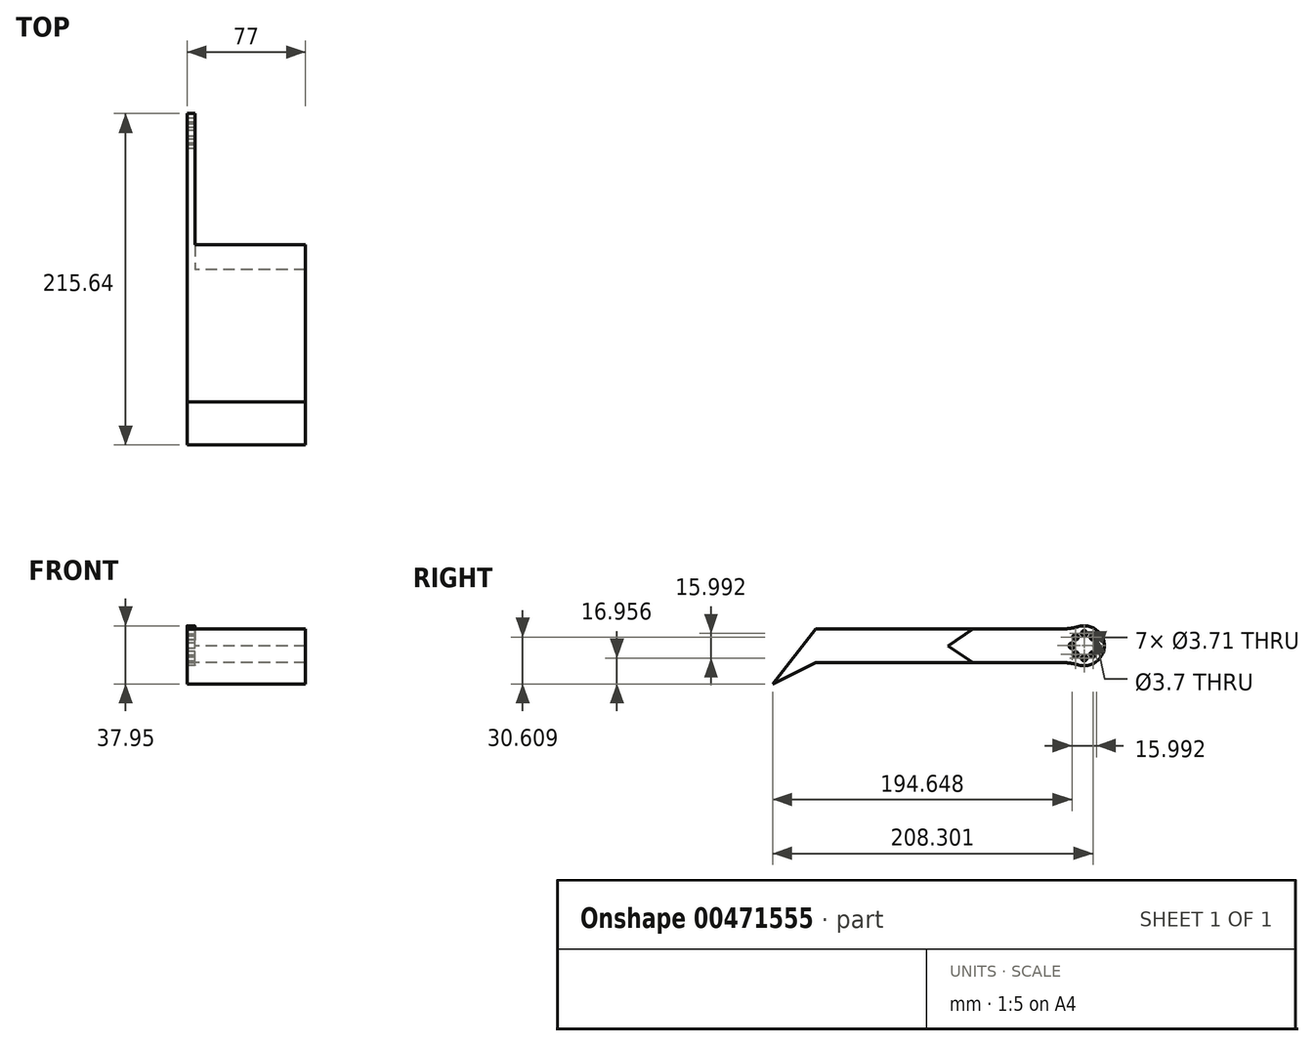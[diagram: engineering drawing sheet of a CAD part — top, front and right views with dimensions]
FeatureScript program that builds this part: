
annotation { "Feature Type Name" : "Feature", "Feature Type Description" : "" }
export const myFeature = defineFeature(function(context is Context, id is Id, definition is map)
    precondition{}
    {
        {
            var Q0;
            Q0=qCreatedBy(makeId("Right.planeOp"),FACE);
            var sketch = newSketch(context, id + "F0", { "sketchPlane" : qUnion([Q0])});
            skLineSegment(sketch, "E0", {"start": v(-42.2, 31.52) * mm, "end": v(60, 31.52) * mm});
            skLineSegment(sketch, "E1", {"start": v(-70.23, -4.43) * mm, "end": v(-42.2, 31.52) * mm});
            skLineSegment(sketch, "E2", {"start": v(-70.23, -4.43) * mm, "end": v(-42.2, 9.51) * mm});
            skLineSegment(sketch, "E3", {"start": v(-42.2, 9.51) * mm, "end": v(60.02, 9.51) * mm});
            skLineSegment(sketch, "E4", {"start": v(60, 31.52) * mm, "end": v(44.03, 20.52) * mm});
            skLineSegment(sketch, "E5", {"start": v(60.02, 9.51) * mm, "end": v(44.03, 20.52) * mm});
            skLineSegment(sketch, "E6", {"start": v(-42.2, 31.52) * mm, "end": v(-42.2, 9.51) * mm, "construction": true});
            skSolve(sketch);
        }
        {
            var Q0;
            Q0=qCreatedBy(makeId("Right.planeOp"),FACE);
            var sketch = newSketch(context, id + "F1", { "sketchPlane" : qUnion([Q0])});
            skLineSegment(sketch, "E7", {"start": v(60, 31.52) * mm, "end": v(125.49, 31.52) * mm});
            skLineSegment(sketch, "E8", {"start": v(125.5, 9.51) * mm, "end": v(60.02, 9.51) * mm});
            skLineSegment(sketch, "E9", {"start": v(60, 31.52) * mm, "end": v(44.03, 20.52) * mm});
            skLineSegment(sketch, "E10", {"start": v(60.02, 9.51) * mm, "end": v(44.03, 20.52) * mm});
            skCircle(sketch, "E11", {"center": v(132.41, 20.52) * mm, "radius": 13 * mm});
            skPoint(sketch, "E11.third.point", {"position": v(145.35, 21.86) * mm});
            skLineSegment(sketch, "E12", {"start": v(132.41, 51.7) * mm, "end": v(132.41, 20.52) * mm, "construction": true});
            skCircle(sketch, "E13", {"center": v(132.41, 28.52) * mm, "radius": 1.85 * mm});
            skPoint(sketch, "E13.first.point", {"position": v(132.41, 30.37) * mm});
            skPoint(sketch, "E13.second.point", {"position": v(132.41, 26.67) * mm});
            skPoint(sketch, "E13.third.point", {"position": v(134.26, 28.4) * mm});
            skLineSegment(sketch, "E14", {"start": v(132.41, 28.52) * mm, "end": v(132.41, 20.52) * mm, "construction": true});
            skLineSegment(sketch, "E15", {"start": v(132.41, 33.52) * mm, "end": v(132.41, 26.67) * mm, "construction": true});
            skLineSegment(sketch, "E16", {"start": v(132.41, 20.52) * mm, "end": v(132.41, 7.52) * mm, "construction": true});
            skCircle(sketch, "E17", {"center": v(132.41, 12.53) * mm, "radius": 1.85 * mm});
            skPoint(sketch, "E17.first.point", {"position": v(132.41, 14.38) * mm});
            skPoint(sketch, "E17.second.point", {"position": v(132.41, 10.67) * mm});
            skPoint(sketch, "E17.third.point", {"position": v(134.26, 12.65) * mm});
            skLineSegment(sketch, "E18", {"start": v(132.41, 14.38) * mm, "end": v(132.41, 12.53) * mm, "construction": true});
            skLineSegment(sketch, "E19", {"start": v(132.41, 14.38) * mm, "end": v(132.41, 7.52) * mm, "construction": true});
            skLineSegment(sketch, "E20", {"start": v(132.41, 20.52) * mm, "end": v(145.41, 20.52) * mm, "construction": true});
            skLineSegment(sketch, "E21", {"start": v(132.41, 20.52) * mm, "end": v(119.41, 20.52) * mm, "construction": true});
            skCircle(sketch, "E22", {"center": v(140.41, 20.52) * mm, "radius": 1.85 * mm});
            skPoint(sketch, "E22.first.point", {"position": v(138.56, 20.52) * mm});
            skPoint(sketch, "E22.second.point", {"position": v(142.26, 20.52) * mm});
            skPoint(sketch, "E22.third.point", {"position": v(140.32, 22.37) * mm});
            skLineSegment(sketch, "E23", {"start": v(140.41, 20.52) * mm, "end": v(132.41, 20.52) * mm, "construction": true});
            skLineSegment(sketch, "E24", {"start": v(138.56, 20.52) * mm, "end": v(145.41, 20.52) * mm, "construction": true});
            skCircle(sketch, "E25", {"center": v(124.42, 20.52) * mm, "radius": 1.85 * mm});
            skPoint(sketch, "E25.first.point", {"position": v(122.56, 20.52) * mm});
            skPoint(sketch, "E25.second.point", {"position": v(126.27, 20.52) * mm});
            skPoint(sketch, "E25.third.point", {"position": v(124.67, 22.36) * mm});
            skLineSegment(sketch, "E26", {"start": v(124.42, 20.52) * mm, "end": v(119.41, 20.52) * mm, "construction": true});
            skLineSegment(sketch, "E27", {"start": v(119.41, 20.52) * mm, "end": v(126.27, 20.52) * mm, "construction": true});
            skPoint(sketch, "E28.1.0", {"position": v(129.34, 25.84) * mm});
            skPoint(sketch, "E28.2.0", {"position": v(129.34, 15.2) * mm});
            skCircle(sketch, "E29.1.0", {"center": v(138.07, 26.18) * mm, "radius": 1.85 * mm});
            skLineSegment(sketch, "E29.anchor1", {"start": v(132.41, 20.52) * mm, "end": v(132.41, 28.52) * mm, "construction": true});
            skLineSegment(sketch, "E29.anchor2", {"start": v(132.41, 20.52) * mm, "end": v(140.41, 20.52) * mm, "construction": true});
            skCircle(sketch, "E30.1.0", {"center": v(138.07, 14.87) * mm, "radius": 1.85 * mm});
            skLineSegment(sketch, "E30.anchor2", {"start": v(132.41, 20.52) * mm, "end": v(132.41, 12.53) * mm, "construction": true});
            skCircle(sketch, "E31.1.0", {"center": v(126.76, 26.18) * mm, "radius": 1.85 * mm});
            skLineSegment(sketch, "E31.anchor1", {"start": v(132.41, 20.52) * mm, "end": v(124.42, 20.52) * mm, "construction": true});
            skCircle(sketch, "E32.1.0", {"center": v(126.76, 14.87) * mm, "radius": 1.85 * mm});
            skSolve(sketch);
        }
        {
            var Q0;
            Q0=makeQuery(id+"F0.imprint","IMPRINT",FACE,{"disambiguationData":[TD([[makeQuery(id+"F0.imprint","IMPRINT",EDGE,{"derivedFrom":sQuery(id+"F0.wireOp",EDGE,"E0")}),-1.0]])]});
            extrude(context, id + "F2", {"entities" : qUnion([Q0]), "depth" : 77 * mm});
        }
        {
            var Q0;
            {var subQ0=sQuery(id+"F1.wireOp",EDGE,"E11");var subQ1=makeQuery(id+"F1.imprint","INTERSECT",VERTEX,{"derivedFrom":[sQuery(id+"F1.wireOp",EDGE,"E7"),subQ0]});Q0=makeQuery(id+"F1.imprint","IMPRINT",FACE,{"disambiguationData":[TD([[makeQuery(id+"F1.imprint","IMPRINT",EDGE,{"disambiguationData":[TD([[subQ1,-1.0]])],"derivedFrom":subQ0}),1.0]])]});}
            var Q1;
            {var subQ1=sQuery(id+"F1.wireOp",EDGE,"E7");Q1=makeQuery(id+"F1.imprint","IMPRINT",FACE,{"disambiguationData":[TD([[makeQuery(id+"F1.imprint","IMPRINT",EDGE,{"derivedFrom":subQ1}),-1.0]])]});}
            extrude(context, id + "F3", {"entities" : qUnion([Q0, Q1]), "operationType" : NewBodyOperationType.ADD, "depth" : 5 * mm});
        }
        {
            var Q0;
            Q0=makeQuery(id+"F3.opExtrude","SWEPT_EDGE",EDGE,{"disambiguationData":[OSD([sQuery(id+"F1.wireOp",EDGE,"E7"),sQuery(id+"F1.wireOp",EDGE,"E11")])]});
            fillet(context, id + "F4", {"entities" : qUnion([Q0]), "radius" : 38.1 * mm, "tangentPropagation" : true, "allowEdgeOverflow" : false});
        }
        {
            var Q0;
            Q0=makeQuery(id+"F3.opExtrude","SWEPT_EDGE",EDGE,{"disambiguationData":[OSD([sQuery(id+"F1.wireOp",EDGE,"E8"),sQuery(id+"F1.wireOp",EDGE,"E11")])]});
            fillet(context, id + "F5", {"entities" : qUnion([Q0]), "radius" : 38.1 * mm, "tangentPropagation" : true, "allowEdgeOverflow" : false});
        }
    });
